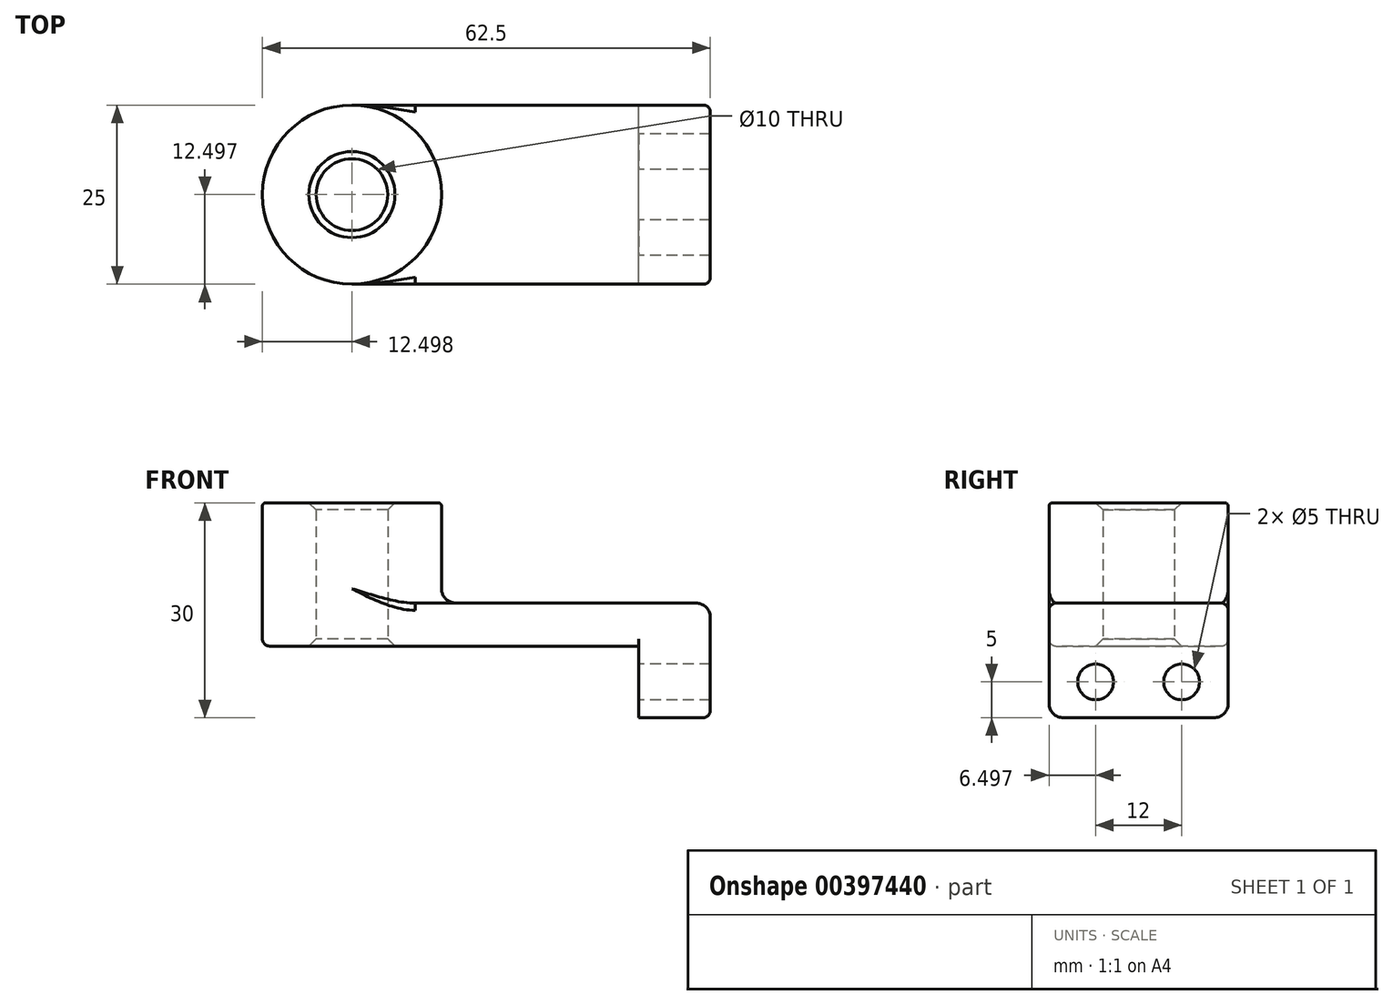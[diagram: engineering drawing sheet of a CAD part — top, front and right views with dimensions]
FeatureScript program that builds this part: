
annotation { "Feature Type Name" : "Feature", "Feature Type Description" : "" }
export const myFeature = defineFeature(function(context is Context, id is Id, definition is map)
    precondition{}
    {
        {
            var Q0;
            Q0=qCreatedBy(makeId("Top.planeOp"),FACE);
            var sketch = newSketch(context, id + "F0", { "sketchPlane" : qUnion([Q0])});
            skLineSegment(sketch, "E0.bottom", {"start": v(13.03, -12.82) * mm, "end": v(-26.97, -12.82) * mm});
            skLineSegment(sketch, "E0.top", {"start": v(13.03, 12.18) * mm, "end": v(-26.97, 12.18) * mm});
            skLineSegment(sketch, "E0.left", {"start": v(13.03, -12.82) * mm, "end": v(13.03, 12.18) * mm});
            skLineSegment(sketch, "E0.right", {"start": v(-26.97, -12.82) * mm, "end": v(-26.97, 12.18) * mm});
            skPoint(sketch, "E0.middle", {"position": v(-6.97, -0.32) * mm});
            skCircle(sketch, "E1", {"center": v(-26.97, -0.32) * mm, "radius": 12.5 * mm});
            skCircle(sketch, "E2", {"center": v(-26.97, -0.32) * mm, "radius": 5 * mm});
            skSolve(sketch);
        }
        {
            var Q0;
            Q0 = qSketchRegion(id + "F0", true);
            extrude(context, id + "F1", {"entities" : qUnion([Q0]), "depth" : 6 * mm});
        }
        {
            var Q0;
            {var subQ1=sQuery(id+"F0.wireOp",EDGE,"E0.right");var subQ3=sQuery(id+"F0.wireOp",EDGE,"E2");var subQ4=makeQuery(id+"F0.imprint","INTERSECT",VERTEX,{"disambiguationData":[OD(0.0)],"derivedFrom":[subQ1,subQ3]});Q0=makeQuery(id+"F0.imprint","IMPRINT",FACE,{"disambiguationData":[TD([[makeQuery(id+"F0.imprint","IMPRINT",EDGE,{"disambiguationData":[TD([[subQ4,-1.0]])],"derivedFrom":subQ3}),-1.0]])]});}
            var Q1;
            {var subQ1=sQuery(id+"F0.wireOp",EDGE,"E0.right");var subQ3=sQuery(id+"F0.wireOp",EDGE,"E2");var subQ4=makeQuery(id+"F0.imprint","INTERSECT",VERTEX,{"disambiguationData":[OD(0.0)],"derivedFrom":[subQ1,subQ3]});Q1=makeQuery(id+"F0.imprint","IMPRINT",FACE,{"disambiguationData":[TD([[makeQuery(id+"F0.imprint","IMPRINT",EDGE,{"disambiguationData":[TD([[subQ4,1.0]])],"derivedFrom":subQ3}),-1.0]])]});}
            extrude(context, id + "F2", {"entities" : qUnion([Q0, Q1]), "operationType" : NewBodyOperationType.ADD, "depth" : 20 * mm});
        }
        {
            var Q0;
            Q0=makeQuery(id+"F1.opExtrude","SWEPT_FACE",FACE,{"disambiguationData":[OSD([sQuery(id+"F0.wireOp",EDGE,"E0.left")])]});
            var sketch = newSketch(context, id + "F3", { "sketchPlane" : qUnion([Q0])});
            skLineSegment(sketch, "E3.bottom", {"start": v(-12.82, 6) * mm, "end": v(12.18, 6) * mm});
            skLineSegment(sketch, "E3.top", {"start": v(-12.82, -10) * mm, "end": v(12.18, -10) * mm});
            skLineSegment(sketch, "E3.left", {"start": v(-12.82, 6) * mm, "end": v(-12.82, -10) * mm});
            skLineSegment(sketch, "E3.right", {"start": v(12.18, 6) * mm, "end": v(12.18, -10) * mm});
            skCircle(sketch, "E4", {"center": v(-6.32, -5) * mm, "radius": 2.5 * mm});
            skLineSegment(sketch, "E5", {"start": v(-0.32, 0) * mm, "end": v(-0.32, -10.32) * mm, "construction": true});
            skCircle(sketch, "E6.MirrorC", {"center": v(5.68, -5) * mm, "radius": 2.5 * mm});
            skSolve(sketch);
        }
        {
            var Q0;
            Q0 = qSketchRegion(id + "F3", true);
            extrude(context, id + "F4", {"entities" : qUnion([Q0]), "operationType" : NewBodyOperationType.ADD, "depth" : 10 * mm});
        }
        {
            var Q0;
            {var subQ0=sQuery(id+"F0.wireOp",EDGE,"E1");Q0=makeQuery(id+"F2.boolean.opBoolean","INTERSECT",EDGE,{"derivedFrom":[makeQuery(id+"F1.opExtrude","CAP_FACE",FACE,{"disambiguationData":[OSD([sQuery(id+"F0.wireOp",EDGE,"E0.bottom"),sQuery(id+"F0.wireOp",EDGE,"E0.top"),sQuery(id+"F0.wireOp",EDGE,"E0.left"),subQ0,sQuery(id+"F0.wireOp",EDGE,"E2")])],"isStart":false}),makeQuery(id+"F2.opExtrude","SWEPT_FACE",FACE,{"disambiguationData":[OSD([subQ0])]})]});}
            var Q1;
            Q1=makeQuery(id+"F4.opExtrude","CAP_EDGE",EDGE,{"disambiguationData":[OSD([sQuery(id+"F3.wireOp",EDGE,"E3.bottom")])],"isStart":false});
            var Q2;
            Q2=makeQuery(id+"F4.opExtrude","SWEPT_EDGE",EDGE,{"disambiguationData":[OSD([sQuery(id+"F3.wireOp",EDGE,"E3.top"),sQuery(id+"F3.wireOp",EDGE,"E3.left")])]});
            var Q3;
            Q3=makeQuery(id+"F4.opExtrude","SWEPT_EDGE",EDGE,{"disambiguationData":[OSD([sQuery(id+"F3.wireOp",EDGE,"E3.top"),sQuery(id+"F3.wireOp",EDGE,"E3.right")])]});
            fillet(context, id + "F5", {"entities" : qUnion([Q0, Q1, Q2, Q3]), "radius" : 2 * mm, "tangentPropagation" : true, "allowEdgeOverflow" : false});
        }
        {
            var Q0;
            Q0=makeQuery(id+"F4.boolean.opBoolean","MERGE",EDGE,{"derivedFrom":[makeQuery(id+"F1.opExtrude","CAP_EDGE",EDGE,{"disambiguationData":[OSD([sQuery(id+"F0.wireOp",EDGE,"E0.bottom")])],"isStart":false}),makeQuery(id+"F4.opExtrude","SWEPT_EDGE",EDGE,{"disambiguationData":[OSD([sQuery(id+"F3.wireOp",EDGE,"E3.bottom"),sQuery(id+"F3.wireOp",EDGE,"E3.left")])]})]});
            var Q1;
            Q1=makeQuery(id+"F1.opExtrude","CAP_EDGE",EDGE,{"disambiguationData":[OSD([sQuery(id+"F0.wireOp",EDGE,"E0.bottom")])],"isStart":true});
            var Q2;
            Q2=makeQuery(id+"F4.boolean.opBoolean","MERGE",EDGE,{"derivedFrom":[makeQuery(id+"F1.opExtrude","CAP_EDGE",EDGE,{"disambiguationData":[OSD([sQuery(id+"F0.wireOp",EDGE,"E0.top")])],"isStart":false}),makeQuery(id+"F4.opExtrude","SWEPT_EDGE",EDGE,{"disambiguationData":[OSD([sQuery(id+"F3.wireOp",EDGE,"E3.bottom"),sQuery(id+"F3.wireOp",EDGE,"E3.right")])]})]});
            var Q3;
            Q3=makeQuery(id+"F1.opExtrude","CAP_EDGE",EDGE,{"disambiguationData":[OSD([sQuery(id+"F0.wireOp",EDGE,"E0.left")])],"isStart":true});
            fillet(context, id + "F6", {"entities" : qUnion([Q0, Q1, Q2, Q3]), "radius" : 1 * mm, "tangentPropagation" : true, "allowEdgeOverflow" : false});
        }
        {
            var Q0;
            {var subQ0=sQuery(id+"F0.wireOp",EDGE,"E2");Q0=makeQuery(id+"F2.boolean.opBoolean","MERGE",FACE,{"derivedFrom":[makeQuery(id+"F1.opExtrude","SWEPT_FACE",FACE,{"disambiguationData":[OSD([subQ0])]}),makeQuery(id+"F2.opExtrude","SWEPT_FACE",FACE,{"disambiguationData":[OSD([subQ0])]})]});}
            chamfer(context, id + "F7", {"entities" : qUnion([Q0]), "width" : 1 * mm, "tangentPropagation" : true});
        }
        {
            var Q0;
            Q0=makeQuery(id+"F2.opExtrude","CAP_EDGE",EDGE,{"disambiguationData":[OSD([sQuery(id+"F0.wireOp",EDGE,"E1")])],"isStart":false});
            fillet(context, id + "F8", {"entities" : qUnion([Q0]), "radius" : 0.5 * mm, "tangentPropagation" : true, "allowEdgeOverflow" : false});
        }
    });
